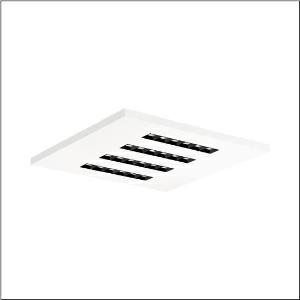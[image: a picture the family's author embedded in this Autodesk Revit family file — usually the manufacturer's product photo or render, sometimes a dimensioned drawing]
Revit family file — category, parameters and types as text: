
# Revit family: silica_r__21_square_51mx6kds44w_0efc
name_source: partatom
category: Lighting Fixtures
units: mm (PartAtom-declared; Revit-internal decimal feet)

## family parameters
Cut with Voids When Loaded = No
Host = Face
Light Source = No
Part Type = Normal
Room Calculation Point = No
Round Connector Dimension = Use Diameter
Shared = No

## types (1)
- --- (1 x LED, 4600 lm, 29.6 W, 4000K)
    Apparent Load = 30 VA
    CIE Flux Codes = 86 100 100 100 100
    Color Rendering = 80
    Color Temperature = 4000K
    Default Elevation = 1800 mm
    Description = Silica® 21 Square, office luminaire, primary light control with lens, of PMMA, primary anti-glare with reflector, of PC, black, CAT 2 (L<= 3000cd/m²), light emission: direct distribution, primary light characteristic: symmetric, installation type: lay-in mounting, LED, rated luminous flux: 4.600lm, luminous efficacy: 155lm/W, light colour: 840, colour temperature: 4000K, with terminal, 5-pole, mains connection: 220..240V, AC, 50/60Hz, rated input power: 29.6W, luminaire housing, of sheet steel, coated, traffic white (RAL 9016), module: M600, length: 597mm, width: 597mm, height: 33mm, protection rating (complete): IP20, insulation class (complete): insulation class I (protective earthing), certification: CE, permissible operating ambient temperature: -20..+40°C, standard: EN 50419, packaging unit: 1 piece
    Height = 0 mm  [stored 0 ft]
    Lamp = 1 x LED
    Lamp Light Flux = 4600 lm
    Lamp Power = 29.6 W
    Lamp count = 1
    Length = 597 mm
    Luminous efficacy = 155 lm/W
    Manufacturer = Siteco
    ModVariant = No
    Model = 51MX6KDS44W
    Mounting Place = Ceiling
    Mounting Type = Recessed
    Number of Poles = 1
    OnlyDefault = Yes
    Power Factor = 1
    Product Name = Silica® 21 Square
    Product group = office luminaire | ceiling recessed
    ProductGroupID = 401
    Protection Class = Protection class I
    Protection Degree = IP 20
    RLX_Detail_Level = 1
    RLX_Emergency_Light_Flux = 0 lm
    RLX_Emergency_Type = 0
    RLX_Emergency_Type_DB = No
    RlxData = <blob elided: 21137 chars, md5=3a11ed63>
    Socket = socket
    Standby Power = 0 W
    System Light Flux = 4600 lm
    System Power = 30 W
    Type Comments = factory setting: luminous flux: 100 % | dim-lin: 254 | 399 mA
    Type Image = l_1275207.jpg
    URL = http://relux.com
    VarID = @adj_036343
    Voltage = 0 V
    Weight = 0.00 kg
    Width = 597 mm

note: [stored X ft] marks values corroborated as IEEE doubles in the binary element streams (Revit-internal decimal feet)

## geometry (parser evidence)
native form markers: Blend x4, Sweep x10
no freeform markers — native parametric forms only
